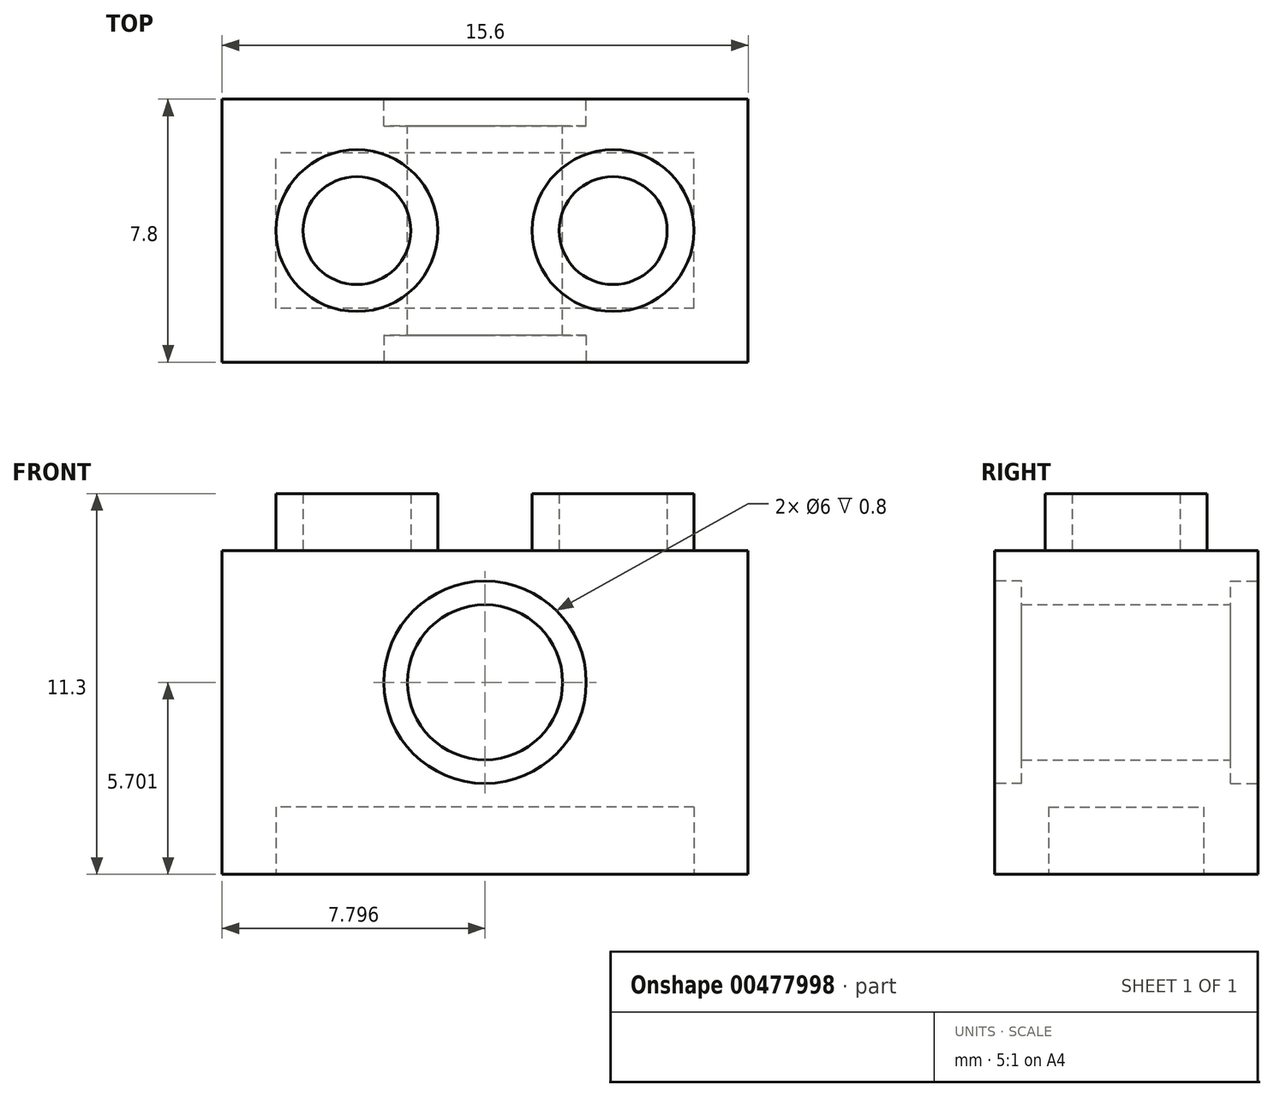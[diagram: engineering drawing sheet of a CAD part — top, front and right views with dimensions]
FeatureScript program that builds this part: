
annotation { "Feature Type Name" : "Feature", "Feature Type Description" : "" }
export const myFeature = defineFeature(function(context is Context, id is Id, definition is map)
    precondition{}
    {
        {
            var Q0;
            Q0=qCreatedBy(makeId("Front.planeOp"),FACE);
            var sketch = newSketch(context, id + "F0", { "sketchPlane" : qUnion([Q0])});
            skLineSegment(sketch, "E0", {"start": v(-13.16, 7.06) * mm, "end": v(-13.16, -2.54) * mm});
            skLineSegment(sketch, "E1", {"start": v(-13.16, -2.54) * mm, "end": v(2.44, -2.54) * mm});
            skLineSegment(sketch, "E2", {"start": v(2.44, -2.54) * mm, "end": v(2.44, 7.06) * mm});
            skLineSegment(sketch, "E3", {"start": v(-13.16, 7.06) * mm, "end": v(2.44, 7.06) * mm});
            skCircle(sketch, "E4", {"center": v(-5.36, 3.16) * mm, "radius": 3 * mm});
            skPoint(sketch, "E4.centerSnap0", {"position": v(-5.36, -2.54) * mm});
            skCircle(sketch, "E5", {"center": v(-5.36, 3.16) * mm, "radius": 2.3 * mm});
            skSolve(sketch);
        }
        {
            var Q0;
            Q0=makeQuery(id+"F0.imprint","IMPRINT",FACE,{"disambiguationData":[TD([[makeQuery(id+"F0.imprint","IMPRINT",EDGE,{"derivedFrom":sQuery(id+"F0.wireOp",EDGE,"E0")}),1.0]])]});
            var Q1;
            Q1=makeQuery(id+"F0.imprint","IMPRINT",FACE,{"disambiguationData":[TD([[makeQuery(id+"F0.imprint","IMPRINT",EDGE,{"derivedFrom":sQuery(id+"F0.wireOp",EDGE,"E4")}),1.0]])]});
            extrude(context, id + "F1", {"entities" : qUnion([Q0, Q1]), "depth" : 7.8 * mm});
        }
        {
            var Q0;
            Q0=makeQuery(id+"F1.opExtrude","SWEPT_FACE",FACE,{"disambiguationData":[OSD([sQuery(id+"F0.wireOp",EDGE,"E3")])]});
            var sketch = newSketch(context, id + "F2", { "sketchPlane" : qUnion([Q0])});
            skCircle(sketch, "E6", {"center": v(-9.16, -3.9) * mm, "radius": 2.4 * mm});
            skPoint(sketch, "E6.centerSnap0", {"position": v(-13.16, -3.9) * mm});
            skCircle(sketch, "E7", {"center": v(-1.56, -3.9) * mm, "radius": 2.4 * mm});
            skPoint(sketch, "E7.centerSnap0", {"position": v(2.44, -3.9) * mm});
            skLineSegment(sketch, "E8", {"start": v(-5.36, 0) * mm, "end": v(-5.36, -7.8) * mm});
            skCircle(sketch, "E9", {"center": v(-9.16, -3.9) * mm, "radius": 1.6 * mm});
            skCircle(sketch, "E10", {"center": v(-1.56, -3.9) * mm, "radius": 1.6 * mm});
            skSolve(sketch);
        }
        {
            var Q0;
            Q0=makeQuery(id+"F2.imprint","IMPRINT",FACE,{"disambiguationData":[TD([[makeQuery(id+"F2.imprint","IMPRINT",EDGE,{"derivedFrom":sQuery(id+"F2.wireOp",EDGE,"E7")}),1.0]])]});
            var Q1;
            Q1=makeQuery(id+"F2.imprint","IMPRINT",FACE,{"disambiguationData":[TD([[makeQuery(id+"F2.imprint","IMPRINT",EDGE,{"derivedFrom":sQuery(id+"F2.wireOp",EDGE,"E6")}),1.0]])]});
            extrude(context, id + "F3", {"entities" : qUnion([Q0, Q1]), "operationType" : NewBodyOperationType.ADD, "depth" : 1.7 * mm});
        }
        {
            var Q0;
            Q0=makeQuery(id+"F1.opExtrude","SWEPT_FACE",FACE,{"disambiguationData":[OSD([sQuery(id+"F0.wireOp",EDGE,"E1")])]});
            var sketch = newSketch(context, id + "F4", { "sketchPlane" : qUnion([Q0])});
            skLineSegment(sketch, "E11", {"start": v(-13.16, 3.9) * mm, "end": v(-11.56, 3.9) * mm});
            skLineSegment(sketch, "E12", {"start": v(-5.36, 7.8) * mm, "end": v(-5.36, 6.2) * mm});
            skLineSegment(sketch, "E13.bottom", {"start": v(0.84, 6.2) * mm, "end": v(-11.56, 6.2) * mm});
            skLineSegment(sketch, "E13.top", {"start": v(0.84, 1.6) * mm, "end": v(-11.56, 1.6) * mm});
            skLineSegment(sketch, "E13.left", {"start": v(0.84, 6.2) * mm, "end": v(0.84, 1.6) * mm});
            skLineSegment(sketch, "E13.right", {"start": v(-11.56, 6.2) * mm, "end": v(-11.56, 1.6) * mm});
            skLineSegment(sketch, "E14.trimOffspring", {"start": v(0.84, 3.9) * mm, "end": v(2.44, 3.9) * mm});
            skLineSegment(sketch, "E15.trimOffspring", {"start": v(-5.36, 1.6) * mm, "end": v(-5.36, 0) * mm});
            skSolve(sketch);
        }
        {
            var Q0;
            {var subQ6=sQuery(id+"F4.wireOp",EDGE,"E13.bottom");var subQ7=makeQuery(id+"F4.imprint","INTERSECT",VERTEX,{"derivedFrom":[sQuery(id+"F4.wireOp",EDGE,"E12"),subQ6]});Q0=makeQuery(id+"F4.imprint","IMPRINT",FACE,{"disambiguationData":[TD([[makeQuery(id+"F4.imprint","IMPRINT",EDGE,{"disambiguationData":[TD([[subQ7,1.0]])],"derivedFrom":subQ6}),1.0]])]});}
            extrude(context, id + "F5", {"entities" : qUnion([Q0]), "operationType" : NewBodyOperationType.REMOVE, "oppositeDirection" : true, "depth" : 2 * mm});
        }
        {
            var Q0;
            Q0=makeQuery(id+"F0.imprint","IMPRINT",FACE,{"disambiguationData":[TD([[makeQuery(id+"F0.imprint","IMPRINT",EDGE,{"derivedFrom":sQuery(id+"F0.wireOp",EDGE,"E4")}),1.0]])]});
            extrude(context, id + "F6", {"entities" : qUnion([Q0]), "operationType" : NewBodyOperationType.REMOVE, "depth" : 0.8 * mm});
        }
        {
            var Q0;
            Q0=makeQuery(id+"F1.opExtrude","CAP_FACE",FACE,{"disambiguationData":[OSD([sQuery(id+"F0.wireOp",EDGE,"E0"),sQuery(id+"F0.wireOp",EDGE,"E1"),sQuery(id+"F0.wireOp",EDGE,"E2"),sQuery(id+"F0.wireOp",EDGE,"E3"),sQuery(id+"F0.wireOp",EDGE,"E5")])],"isStart":false});
            var sketch = newSketch(context, id + "F7", { "sketchPlane" : qUnion([Q0])});
            skLineSegment(sketch, "E16", {"start": v(-13.16, 7.06) * mm, "end": v(-13.16, -2.54) * mm});
            skLineSegment(sketch, "E17", {"start": v(-13.16, -2.54) * mm, "end": v(2.44, -2.54) * mm});
            skLineSegment(sketch, "E18", {"start": v(2.44, -2.54) * mm, "end": v(2.44, 7.06) * mm});
            skLineSegment(sketch, "E19", {"start": v(-13.16, 7.06) * mm, "end": v(2.44, 7.06) * mm});
            skCircle(sketch, "E20", {"center": v(-5.36, 3.16) * mm, "radius": 3 * mm});
            skPoint(sketch, "E20.centerSnap0", {"position": v(-5.36, -2.54) * mm});
            skCircle(sketch, "E21", {"center": v(-5.36, 3.16) * mm, "radius": 2.3 * mm});
            skSolve(sketch);
        }
        {
            var Q0;
            Q0=makeQuery(id+"F7.imprint","IMPRINT",FACE,{"disambiguationData":[TD([[makeQuery(id+"F7.imprint","IMPRINT",EDGE,{"derivedFrom":sQuery(id+"F7.wireOp",EDGE,"E20")}),1.0]])]});
            extrude(context, id + "F8", {"entities" : qUnion([Q0]), "operationType" : NewBodyOperationType.REMOVE, "oppositeDirection" : true, "depth" : 0.8 * mm});
        }
    });
